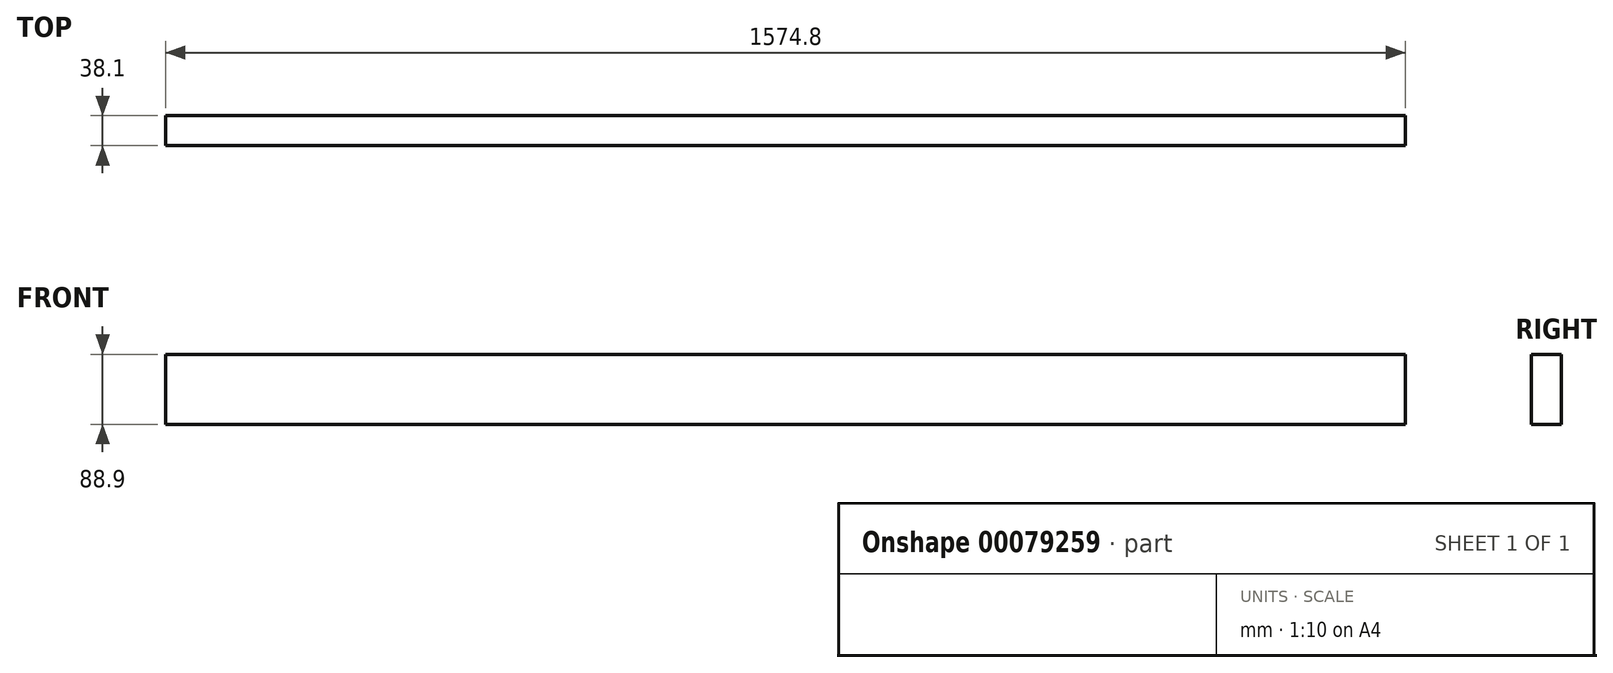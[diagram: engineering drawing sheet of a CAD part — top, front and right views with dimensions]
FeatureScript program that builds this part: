
annotation { "Feature Type Name" : "Feature", "Feature Type Description" : "" }
export const myFeature = defineFeature(function(context is Context, id is Id, definition is map)
    precondition{}
    {
        {
            var Q0;
            Q0=qCreatedBy(makeId("Right.planeOp"),FACE);
            var sketch = newSketch(context, id + "F0", { "sketchPlane" : qUnion([Q0])});
            skLineSegment(sketch, "E0.bottom", {"start": v(0, 0) * mm, "end": v(-38.1, 0) * mm});
            skLineSegment(sketch, "E0.top", {"start": v(0, 88.9) * mm, "end": v(-38.1, 88.9) * mm});
            skLineSegment(sketch, "E0.left", {"start": v(0, 0) * mm, "end": v(0, 88.9) * mm});
            skLineSegment(sketch, "E0.right", {"start": v(-38.1, 0) * mm, "end": v(-38.1, 88.9) * mm});
            skSolve(sketch);
        }
        {
            var Q0;
            Q0=makeQuery(id+"F0.imprint","IMPRINT",FACE,{"disambiguationData":[TD([[makeQuery(id+"F0.imprint","IMPRINT",EDGE,{"derivedFrom":sQuery(id+"F0.wireOp",EDGE,"E0.bottom")}),-1.0]])]});
            extrude(context, id + "F1", {"entities" : qUnion([Q0]), "depth" : 1574.8 * mm});
        }
    });
